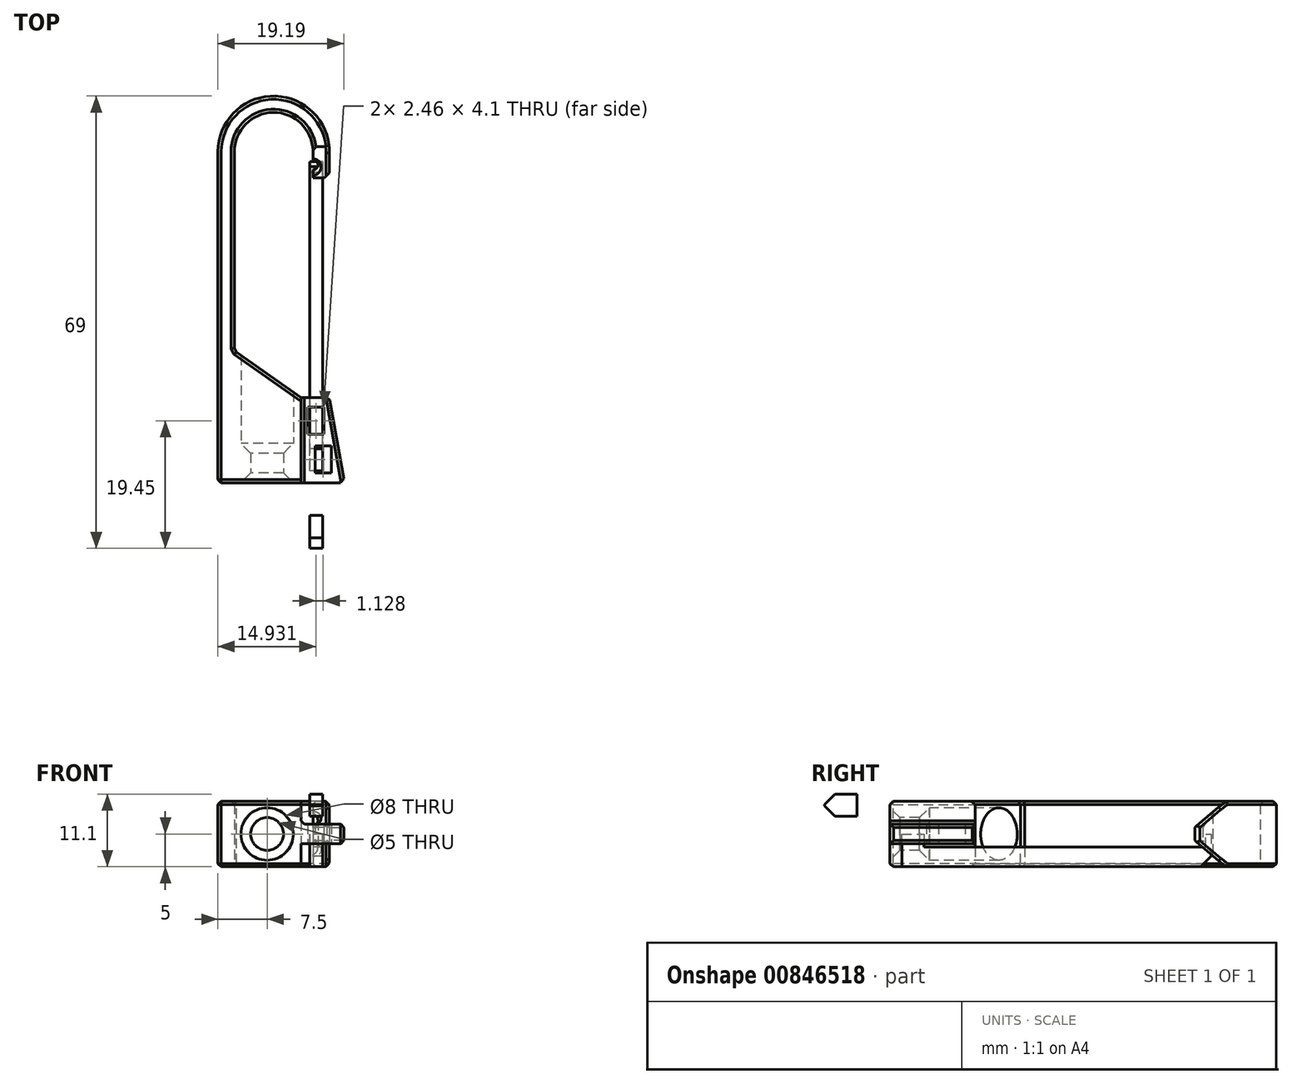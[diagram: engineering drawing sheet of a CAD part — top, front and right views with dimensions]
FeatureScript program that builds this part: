
annotation { "Feature Type Name" : "Feature", "Feature Type Description" : "" }
export const myFeature = defineFeature(function(context is Context, id is Id, definition is map)
    precondition{}
    {
        {
            var Q0;
            Q0=qCreatedBy(makeId("Top.planeOp"),FACE);
            var sketch = newSketch(context, id + "F0", { "sketchPlane" : qUnion([Q0])});
            skCircle(sketch, "E0", {"center": v(-1, -1.5) * mm, "radius": 4 * mm});
            skLineSegment(sketch, "E1.bottom", {"start": v(-8.5, 3.5) * mm, "end": v(8.5, 3.5) * mm});
            skLineSegment(sketch, "E1.top", {"start": v(-8.5, -6.5) * mm, "end": v(8.5, -6.5) * mm});
            skLineSegment(sketch, "E1.left", {"start": v(-8.5, 3.5) * mm, "end": v(-8.5, -6.5) * mm});
            skLineSegment(sketch, "E1.right", {"start": v(8.5, 3.5) * mm, "end": v(8.5, -6.5) * mm});
            skPoint(sketch, "E1.middle", {"position": v(0, -1.5) * mm});
            skCircle(sketch, "E2", {"center": v(-1, -1.5) * mm, "radius": 2.5 * mm});
            skSolve(sketch);
        }
        {
            var Q0;
            Q0=qCreatedBy(makeId("Front.planeOp"),FACE);
            cPlane(context, id + "F1", {"entities" : qUnion([Q0]), "cplaneType" : CPlaneType.OFFSET, "offset" : 3.5 * mm, "oppositeDirection" : true, "width" : 150 * mm, "height" : 150 * mm});
        }
        {
            var Q0;
            Q0=qCreatedBy(id+"F1.planeOp",FACE);
            var sketch = newSketch(context, id + "F2", { "sketchPlane" : qUnion([Q0])});
            skLineSegment(sketch, "E3", {"start": v(0, 0) * mm, "end": v(8.5, 0) * mm});
            skLineSegment(sketch, "E4.MirrorCS", {"start": v(0, 0) * mm, "end": v(-8.5, 0) * mm});
            skLineSegment(sketch, "E5", {"start": v(8.5, 0) * mm, "end": v(8.5, 13) * mm});
            skLineSegment(sketch, "E6", {"start": v(8.5, 13) * mm, "end": v(4.2, 13) * mm});
            skLineSegment(sketch, "E7", {"start": v(4.2, 13) * mm, "end": v(-6, 20.14) * mm});
            skLineSegment(sketch, "E8", {"start": v(-8.5, 0) * mm, "end": v(-8.5, 50.5) * mm});
            skLineSegment(sketch, "E9", {"start": v(-6, 20.14) * mm, "end": v(-6, 50.5) * mm});
            skLineSegment(sketch, "E10", {"start": v(-6, 50.5) * mm, "end": v(0, 50.5) * mm});
            skArc(sketch, "E11", {"start": v(8.5, 50.5) * mm, "mid": v(0, 59) * mm, "end": v(-8.5, 50.5) * mm});
            skArc(sketch, "E12", {"start": v(6, 50.5) * mm, "mid": v(0, 56.5) * mm, "end": v(-6, 50.5) * mm});
            skLineSegment(sketch, "E13", {"start": v(0, 50.5) * mm, "end": v(8.5, 50.5) * mm});
            skLineSegment(sketch, "E14", {"start": v(6, 50.5) * mm, "end": v(6, 46.5) * mm});
            skLineSegment(sketch, "E15.bottom", {"start": v(6, 46.5) * mm, "end": v(8.5, 46.5) * mm});
            skLineSegment(sketch, "E15.top", {"start": v(6, 50.5) * mm, "end": v(8.5, 50.5) * mm});
            skLineSegment(sketch, "E15.left", {"start": v(6, 46.5) * mm, "end": v(6, 50.5) * mm});
            skLineSegment(sketch, "E15.right", {"start": v(8.5, 46.5) * mm, "end": v(8.5, 50.5) * mm});
            skCircle(sketch, "E16", {"center": v(8.5, 48.5) * mm, "radius": 0.75 * mm});
            skLineSegment(sketch, "E17", {"start": v(8.5, 13) * mm, "end": v(10.8, 0) * mm});
            skLineSegment(sketch, "E18", {"start": v(10.8, 0) * mm, "end": v(8.5, 0) * mm});
            skLineSegment(sketch, "E19", {"start": v(4.2, 13) * mm, "end": v(4.2, 0) * mm});
            skLineSegment(sketch, "E20.0", {"start": v(5.2, 12) * mm, "end": v(5.2, 0) * mm});
            skLineSegment(sketch, "E20.1", {"start": v(7.66, 12) * mm, "end": v(5.2, 12) * mm});
            skLineSegment(sketch, "E20.2", {"start": v(7.66, 12) * mm, "end": v(9.6, 1) * mm});
            skLineSegment(sketch, "E20.3", {"start": v(9.6, 1) * mm, "end": v(8.5, 1) * mm});
            skLineSegment(sketch, "E21", {"start": v(8.5, 1) * mm, "end": v(5.2, 1) * mm});
            skLineSegment(sketch, "E22", {"start": v(5.2, 12) * mm, "end": v(7.14, 1) * mm});
            skCircle(sketch, "E23", {"center": v(6, 48.5) * mm, "radius": 0.75 * mm});
            skLineSegment(sketch, "E24.0", {"start": v(8.5, 11.5) * mm, "end": v(4.2, 11.5) * mm});
            skLineSegment(sketch, "E25.0", {"start": v(0, 1.5) * mm, "end": v(8.5, 1.5) * mm});
            skLineSegment(sketch, "E25.1", {"start": v(10.8, 1.5) * mm, "end": v(8.5, 1.5) * mm});
            skLineSegment(sketch, "E26", {"start": v(8.79, 5.6) * mm, "end": v(8.79, 1) * mm});
            skLineSegment(sketch, "E27", {"start": v(8.79, 5.6) * mm, "end": v(6.33, 5.6) * mm});
            skLineSegment(sketch, "E28", {"start": v(7.66, 12) * mm, "end": v(7.66, 7.4) * mm});
            skLineSegment(sketch, "E29", {"start": v(7.66, 7.4) * mm, "end": v(5.2, 7.4) * mm});
            skLineSegment(sketch, "E30", {"start": v(6.33, 5.6) * mm, "end": v(6.33, 1) * mm});
            skSolve(sketch);
        }
        {
            var Q0;
            {var subQ1=sQuery(id+"F2.wireOp",EDGE,"E6");Q0=makeQuery(id+"F2.imprint","IMPRINT",FACE,{"disambiguationData":[TD([[makeQuery(id+"F2.imprint","IMPRINT",EDGE,{"derivedFrom":subQ1}),1.0]])]});}
            var Q1;
            {var subQ0=sQuery(id+"F2.wireOp",EDGE,"E24.0");var subQ1=sQuery(id+"F2.wireOp",EDGE,"E19");var subQ2=makeQuery(id+"F2.imprint","INTERSECT",VERTEX,{"derivedFrom":[subQ1,subQ0]});Q1=makeQuery(id+"F2.imprint","IMPRINT",FACE,{"disambiguationData":[TD([[makeQuery(id+"F2.imprint","IMPRINT",EDGE,{"disambiguationData":[TD([[subQ2,-1.0]])],"derivedFrom":subQ1}),1.0]])]});}
            var Q2;
            {var subQ4=sQuery(id+"F2.wireOp",EDGE,"E3");var subQ6=sQuery(id+"F2.wireOp",EDGE,"E19");var subQ7=makeQuery(id+"F2.imprint","INTERSECT",VERTEX,{"derivedFrom":[subQ4,subQ6]});Q2=makeQuery(id+"F2.imprint","IMPRINT",FACE,{"disambiguationData":[TD([[makeQuery(id+"F2.imprint","IMPRINT",EDGE,{"disambiguationData":[TD([[subQ7,-1.0]])],"derivedFrom":subQ4}),1.0]])]});}
            var Q3;
            {var subQ0=sQuery(id+"F2.wireOp",EDGE,"E20.0");var subQ1=sQuery(id+"F2.wireOp",EDGE,"E3");var subQ2=makeQuery(id+"F2.imprint","INTERSECT",VERTEX,{"derivedFrom":[subQ1,subQ0]});Q3=makeQuery(id+"F2.imprint","IMPRINT",FACE,{"disambiguationData":[TD([[makeQuery(id+"F2.imprint","IMPRINT",EDGE,{"disambiguationData":[TD([[subQ2,1.0]])],"derivedFrom":subQ0}),1.0]])]});}
            var Q4;
            {var subQ0=sQuery(id+"F2.wireOp",EDGE,"E18");Q4=makeQuery(id+"F2.imprint","IMPRINT",FACE,{"disambiguationData":[TD([[makeQuery(id+"F2.imprint","IMPRINT",EDGE,{"derivedFrom":subQ0}),-1.0]])]});}
            var Q5;
            {var subQ2=sQuery(id+"F2.wireOp",EDGE,"E5");var subQ6=makeQuery(id+"F2.imprint","INTERSECT",VERTEX,{"derivedFrom":[subQ2,sQuery(id+"F2.wireOp",EDGE,"E24.0")]});Q5=makeQuery(id+"F2.imprint","IMPRINT",FACE,{"disambiguationData":[TD([[makeQuery(id+"F2.imprint","IMPRINT",EDGE,{"disambiguationData":[TD([[subQ6,1.0]])],"derivedFrom":subQ2}),-1.0]])]});}
            var Q6;
            {var subQ4=sQuery(id+"F2.wireOp",EDGE,"E4.MirrorCS");Q6=makeQuery(id+"F2.imprint","IMPRINT",FACE,{"disambiguationData":[TD([[makeQuery(id+"F2.imprint","IMPRINT",EDGE,{"derivedFrom":subQ4}),-1.0]])]});}
            var Q7;
            {var subQ5=sQuery(id+"F2.wireOp",EDGE,"E5");var subQ7=sQuery(id+"F2.wireOp",EDGE,"E27");var subQ13=makeQuery(id+"F2.imprint","INTERSECT",VERTEX,{"derivedFrom":[subQ5,subQ7]});Q7=makeQuery(id+"F2.imprint","IMPRINT",FACE,{"disambiguationData":[TD([[makeQuery(id+"F2.imprint","IMPRINT",EDGE,{"disambiguationData":[TD([[subQ13,-1.0]])],"derivedFrom":subQ5}),1.0]])]});}
            var Q8;
            {var subQ1=sQuery(id+"F2.wireOp",EDGE,"E20.0");var subQ7=sQuery(id+"F2.wireOp",EDGE,"E29");var subQ9=makeQuery(id+"F2.imprint","INTERSECT",VERTEX,{"derivedFrom":[subQ1,subQ7]});Q8=makeQuery(id+"F2.imprint","IMPRINT",FACE,{"disambiguationData":[TD([[makeQuery(id+"F2.imprint","IMPRINT",EDGE,{"disambiguationData":[TD([[subQ9,-1.0]])],"derivedFrom":subQ1}),1.0]])]});}
            var Q9;
            {var subQ1=sQuery(id+"F2.wireOp",EDGE,"E20.2");var subQ3=sQuery(id+"F2.wireOp",EDGE,"E24.0");var subQ4=makeQuery(id+"F2.imprint","INTERSECT",VERTEX,{"derivedFrom":[subQ1,subQ3]});Q9=makeQuery(id+"F2.imprint","IMPRINT",FACE,{"disambiguationData":[TD([[makeQuery(id+"F2.imprint","IMPRINT",EDGE,{"disambiguationData":[TD([[subQ4,-1.0]])],"derivedFrom":subQ3}),-1.0]])]});}
            var Q10;
            {var subQ0=sQuery(id+"F2.wireOp",EDGE,"E24.0");var subQ1=sQuery(id+"F2.wireOp",EDGE,"E5");var subQ2=makeQuery(id+"F2.imprint","INTERSECT",VERTEX,{"derivedFrom":[subQ1,subQ0]});Q10=makeQuery(id+"F2.imprint","IMPRINT",FACE,{"disambiguationData":[TD([[makeQuery(id+"F2.imprint","IMPRINT",EDGE,{"disambiguationData":[TD([[subQ2,1.0]])],"derivedFrom":subQ1}),1.0]])]});}
            var Q11;
            {var subQ0=sQuery(id+"F2.wireOp",EDGE,"E21");var subQ1=sQuery(id+"F2.wireOp",EDGE,"E20.0");var subQ2=makeQuery(id+"F2.imprint","INTERSECT",VERTEX,{"derivedFrom":[subQ1,subQ0]});Q11=makeQuery(id+"F2.imprint","IMPRINT",FACE,{"disambiguationData":[TD([[makeQuery(id+"F2.imprint","IMPRINT",EDGE,{"disambiguationData":[TD([[subQ2,1.0]])],"derivedFrom":subQ1}),1.0]])]});}
            var Q12;
            {var subQ4=sQuery(id+"F2.wireOp",EDGE,"E15.bottom");Q12=makeQuery(id+"F2.imprint","IMPRINT",FACE,{"disambiguationData":[TD([[makeQuery(id+"F2.imprint","IMPRINT",EDGE,{"derivedFrom":subQ4}),1.0]])]});}
            var Q13;
            {var subQ0=sQuery(id+"F2.wireOp",EDGE,"E16");var subQ1=sQuery(id+"F2.wireOp",EDGE,"E15.right");var subQ2=makeQuery(id+"F2.imprint","INTERSECT",VERTEX,{"disambiguationData":[OD(0.0)],"derivedFrom":[subQ1,subQ0]});Q13=makeQuery(id+"F2.imprint","IMPRINT",FACE,{"disambiguationData":[TD([[makeQuery(id+"F2.imprint","IMPRINT",EDGE,{"disambiguationData":[TD([[subQ2,-1.0]])],"derivedFrom":subQ1}),1.0]])]});}
            var Q14;
            {var subQ1=sQuery(id+"F2.wireOp",EDGE,"E20.2");var subQ3=sQuery(id+"F2.wireOp",EDGE,"E25.1");var subQ4=makeQuery(id+"F2.imprint","INTERSECT",VERTEX,{"derivedFrom":[subQ1,subQ3]});Q14=makeQuery(id+"F2.imprint","IMPRINT",FACE,{"disambiguationData":[TD([[makeQuery(id+"F2.imprint","IMPRINT",EDGE,{"disambiguationData":[TD([[subQ4,-1.0]])],"derivedFrom":subQ3}),-1.0]])]});}
            var Q15;
            {var subQ0=sQuery(id+"F2.wireOp",EDGE,"E20.3");var subQ1=sQuery(id+"F2.wireOp",EDGE,"E20.2");var subQ2=makeQuery(id+"F2.imprint","INTERSECT",VERTEX,{"derivedFrom":[subQ1,subQ0]});Q15=makeQuery(id+"F2.imprint","IMPRINT",FACE,{"disambiguationData":[TD([[makeQuery(id+"F2.imprint","IMPRINT",EDGE,{"disambiguationData":[TD([[subQ2,1.0]])],"derivedFrom":subQ1}),-1.0]])]});}
            var Q16;
            {var subQ0=sQuery(id+"F2.wireOp",EDGE,"E27");var subQ1=sQuery(id+"F2.wireOp",EDGE,"E5");var subQ2=makeQuery(id+"F2.imprint","INTERSECT",VERTEX,{"derivedFrom":[subQ1,subQ0]});Q16=makeQuery(id+"F2.imprint","IMPRINT",FACE,{"disambiguationData":[TD([[makeQuery(id+"F2.imprint","IMPRINT",EDGE,{"disambiguationData":[TD([[subQ2,-1.0]])],"derivedFrom":subQ1}),-1.0]])]});}
            var Q17;
            {var subQ0=sQuery(id+"F2.wireOp",EDGE,"E22");var subQ1=sQuery(id+"F2.wireOp",EDGE,"E21");var subQ2=makeQuery(id+"F2.imprint","INTERSECT",VERTEX,{"derivedFrom":[subQ1,subQ0]});Q17=makeQuery(id+"F2.imprint","IMPRINT",FACE,{"disambiguationData":[TD([[makeQuery(id+"F2.imprint","IMPRINT",EDGE,{"disambiguationData":[TD([[subQ2,-1.0]])],"derivedFrom":subQ1}),-1.0]])]});}
            var Q18;
            {var subQ0=sQuery(id+"F2.wireOp",EDGE,"E21");var subQ5=sQuery(id+"F2.wireOp",EDGE,"E22");var subQ7=makeQuery(id+"F2.imprint","INTERSECT",VERTEX,{"derivedFrom":[subQ0,subQ5]});Q18=makeQuery(id+"F2.imprint","IMPRINT",FACE,{"disambiguationData":[TD([[makeQuery(id+"F2.imprint","IMPRINT",EDGE,{"disambiguationData":[TD([[subQ7,1.0]])],"derivedFrom":subQ5}),1.0]])]});}
            var Q19;
            {var subQ0=sQuery(id+"F2.wireOp",EDGE,"E20.3");var subQ5=sQuery(id+"F2.wireOp",EDGE,"E26");var subQ6=makeQuery(id+"F2.imprint","INTERSECT",VERTEX,{"derivedFrom":[subQ0,subQ5]});Q19=makeQuery(id+"F2.imprint","IMPRINT",FACE,{"disambiguationData":[TD([[makeQuery(id+"F2.imprint","IMPRINT",EDGE,{"disambiguationData":[TD([[subQ6,1.0]])],"derivedFrom":subQ5}),-1.0]])]});}
            var Q20;
            {var subQ0=sQuery(id+"F2.wireOp",EDGE,"E20.1");Q20=makeQuery(id+"F2.imprint","IMPRINT",FACE,{"disambiguationData":[TD([[makeQuery(id+"F2.imprint","IMPRINT",EDGE,{"derivedFrom":subQ0}),1.0]])]});}
            var Q21;
            {var subQ1=sQuery(id+"F2.wireOp",EDGE,"E20.0");var subQ3=sQuery(id+"F2.wireOp",EDGE,"E24.0");var subQ4=makeQuery(id+"F2.imprint","INTERSECT",VERTEX,{"derivedFrom":[subQ1,subQ3]});Q21=makeQuery(id+"F2.imprint","IMPRINT",FACE,{"disambiguationData":[TD([[makeQuery(id+"F2.imprint","IMPRINT",EDGE,{"disambiguationData":[TD([[subQ4,1.0]])],"derivedFrom":subQ3}),-1.0]])]});}
            var Q22;
            {var subQ1=sQuery(id+"F2.wireOp",EDGE,"E20.2");var subQ3=sQuery(id+"F2.wireOp",EDGE,"E24.0");var subQ4=makeQuery(id+"F2.imprint","INTERSECT",VERTEX,{"derivedFrom":[subQ1,subQ3]});Q22=makeQuery(id+"F2.imprint","IMPRINT",FACE,{"disambiguationData":[TD([[makeQuery(id+"F2.imprint","IMPRINT",EDGE,{"disambiguationData":[TD([[subQ4,-1.0]])],"derivedFrom":subQ3}),-1.0]])]});}
            extrude(context, id + "F3", {"entities" : qUnion([Q0, Q1, Q2, Q3, Q4, Q5, Q6, Q7, Q8, Q9, Q10, Q11, Q12, Q13, Q14, Q15, Q16, Q17, Q18, Q19, Q20, Q21, Q22]), "depth" : 10 * mm, "offsetDistance" : 25 * mm});
        }
        {
            var Q0;
            Q0=makeQuery(id+"F0.imprint","IMPRINT",FACE,{"disambiguationData":[TD([[makeQuery(id+"F0.imprint","IMPRINT",EDGE,{"derivedFrom":sQuery(id+"F0.wireOp",EDGE,"E0")}),1.0]])]});
            var Q1;
            Q1=makeQuery(id+"F0.imprint","IMPRINT",FACE,{"disambiguationData":[TD([[makeQuery(id+"F0.imprint","IMPRINT",EDGE,{"derivedFrom":sQuery(id+"F0.wireOp",EDGE,"E2")}),1.0]])]});
            extrude(context, id + "F4", {"entities" : qUnion([Q0, Q1]), "operationType" : NewBodyOperationType.REMOVE, "depth" : 25 * mm, "offsetDistance" : 25 * mm});
        }
        {
            var Q0;
            Q0=makeQuery(id+"F0.imprint","IMPRINT",FACE,{"disambiguationData":[TD([[makeQuery(id+"F0.imprint","IMPRINT",EDGE,{"derivedFrom":sQuery(id+"F0.wireOp",EDGE,"E0")}),1.0]])]});
            extrude(context, id + "F5", {"entities" : qUnion([Q0]), "operationType" : NewBodyOperationType.ADD, "depth" : 6 * mm, "offsetDistance" : 25 * mm});
        }
        {
            var Q0;
            Q0=makeQuery(id+"F3.opExtrude","CAP_EDGE",EDGE,{"disambiguationData":[OSD([sQuery(id+"F2.wireOp",EDGE,"E15.bottom")])],"isStart":false});
            var Q1;
            Q1=makeQuery(id+"F3.opExtrude","CAP_EDGE",EDGE,{"disambiguationData":[OSD([sQuery(id+"F2.wireOp",EDGE,"E15.bottom")])],"isStart":true});
            chamfer(context, id + "F6", {"entities" : qUnion([Q0, Q1]), "chamferType" : ChamferType.OFFSET_ANGLE, "width" : 4 * mm, "oppositeDirection" : true, "angle" : 50 * degree, "tangentPropagation" : true});
        }
        {
            var Q0;
            Q0=makeQuery(id+"F5.opExtrude","CAP_EDGE",EDGE,{"disambiguationData":[OSD([sQuery(id+"F0.wireOp",EDGE,"E2")])],"isStart":true});
            var Q1;
            Q1=makeQuery(id+"F5.opExtrude","CAP_EDGE",EDGE,{"disambiguationData":[OSD([sQuery(id+"F0.wireOp",EDGE,"E2")])],"isStart":false});
            chamfer(context, id + "F7", {"entities" : qUnion([Q0, Q1]), "width" : 1.5 * mm, "tangentPropagation" : true});
        }
        {
            var Q0;
            Q0=makeQuery(id+"F3.opExtrude","SWEPT_EDGE",EDGE,{"disambiguationData":[OSD([sQuery(id+"F2.wireOp",EDGE,"E7"),sQuery(id+"F2.wireOp",EDGE,"E9")])]});
            var Q1;
            Q1=makeQuery(id+"F3.opExtrude","SWEPT_EDGE",EDGE,{"disambiguationData":[OSD([sQuery(id+"F2.wireOp",EDGE,"E15.bottom"),sQuery(id+"F2.wireOp",EDGE,"E15.right")])]});
            chamfer(context, id + "F8", {"entities" : qUnion([Q0, Q1]), "width" : .8 * mm, "tangentPropagation" : true});
        }
        {
            var Q0;
            Q0=qCreatedBy(id+"F1.planeOp",FACE);
            var sketch = newSketch(context, id + "F9", { "sketchPlane" : qUnion([Q0])});
            skLineSegment(sketch, "E31", {"start": v(0, 0) * mm, "end": v(4.2, 0) * mm});
            skLineSegment(sketch, "E32", {"start": v(4.2, 0) * mm, "end": v(11.2, 0) * mm});
            skLineSegment(sketch, "E33", {"start": v(4.2, 0) * mm, "end": v(4.2, 15.17) * mm});
            skLineSegment(sketch, "E34.bottom", {"start": v(4.2, 15.17) * mm, "end": v(11.2, 15.17) * mm});
            skLineSegment(sketch, "E34.left", {"start": v(4.2, 15.17) * mm, "end": v(4.2, 0) * mm});
            skLineSegment(sketch, "E34.right", {"start": v(11.2, 15.17) * mm, "end": v(11.2, 0) * mm});
            skSolve(sketch);
        }
        {
            var Q0;
            Q0=qSketchRegion(id+"F9",true);
            extrude(context, id + "F10", {"entities" : qUnion([Q0]), "operationType" : NewBodyOperationType.REMOVE, "depth" : 3.5 * mm, "offsetDistance" : 25 * mm});
        }
        {
            var Q0;
            Q0=qCreatedBy(id+"F1.planeOp",FACE);
            cPlane(context, id + "F11", {"entities" : qUnion([Q0]), "cplaneType" : CPlaneType.OFFSET, "offset" : 10 * mm, "width" : 150 * mm, "height" : 150 * mm});
        }
        {
            var Q0;
            Q0=qCreatedBy(id+"F11.planeOp",FACE);
            var sketch = newSketch(context, id + "F12", { "sketchPlane" : qUnion([Q0])});
            skLineSegment(sketch, "E35", {"start": v(0, 0) * mm, "end": v(4.2, 0) * mm});
            skLineSegment(sketch, "E36", {"start": v(4.2, 0) * mm, "end": v(11.2, 0) * mm});
            skLineSegment(sketch, "E37", {"start": v(11.2, 0) * mm, "end": v(11.2, 14.54) * mm});
            skLineSegment(sketch, "E38.bottom", {"start": v(11.2, 14.54) * mm, "end": v(4.2, 14.54) * mm});
            skLineSegment(sketch, "E38.top", {"start": v(11.2, 0) * mm, "end": v(4.2, 0) * mm});
            skLineSegment(sketch, "E38.left", {"start": v(11.2, 14.54) * mm, "end": v(11.2, 0) * mm});
            skLineSegment(sketch, "E38.right", {"start": v(4.2, 14.54) * mm, "end": v(4.2, 0) * mm});
            skSolve(sketch);
        }
        {
            var Q0;
            Q0=qSketchRegion(id+"F12",true);
            extrude(context, id + "F13", {"entities" : qUnion([Q0]), "operationType" : NewBodyOperationType.REMOVE, "oppositeDirection" : true, "depth" : 3.5 * mm, "offsetDistance" : 25 * mm});
        }
        {
            var Q0;
            Q0=makeQuery(id+"F13.boolean.opBoolean","INTERSECT",EDGE,{"derivedFrom":[makeQuery(id+"F3.opExtrude","SWEPT_FACE",FACE,{"disambiguationData":[OSD([sQuery(id+"F2.wireOp",EDGE,"E17")])]}),makeQuery(id+"F13.opExtrude","CAP_FACE",FACE,{"disambiguationData":[OSD([sQuery(id+"F12.wireOp",EDGE,"E38.bottom"),sQuery(id+"F12.wireOp",EDGE,"E38.top"),sQuery(id+"F12.wireOp",EDGE,"E38.left"),sQuery(id+"F12.wireOp",EDGE,"E38.right")])],"isStart":false})]});
            var Q1;
            Q1=makeQuery(id+"F10.boolean.opBoolean","INTERSECT",EDGE,{"derivedFrom":[makeQuery(id+"F3.opExtrude","SWEPT_FACE",FACE,{"disambiguationData":[OSD([sQuery(id+"F2.wireOp",EDGE,"E17")])]}),makeQuery(id+"F10.opExtrude","CAP_FACE",FACE,{"disambiguationData":[OSD([sQuery(id+"F9.wireOp",EDGE,"E34.bottom"),sQuery(id+"F9.wireOp",EDGE,"E32"),sQuery(id+"F9.wireOp",EDGE,"E34.left"),sQuery(id+"F9.wireOp",EDGE,"E34.right")])],"isStart":false})]});
            var Q2;
            Q2=makeQuery(id+"F3.opExtrude","CAP_EDGE",EDGE,{"disambiguationData":[OSD([sQuery(id+"F2.wireOp",EDGE,"E8")])],"isStart":false});
            var Q3;
            Q3=makeQuery(id+"F3.opExtrude","CAP_EDGE",EDGE,{"disambiguationData":[OSD([sQuery(id+"F2.wireOp",EDGE,"E8")])],"isStart":true});
            var Q4;
            Q4=makeQuery(id+"F3.opExtrude","CAP_EDGE",EDGE,{"disambiguationData":[OSD([sQuery(id+"F2.wireOp",EDGE,"E9")])],"isStart":true});
            var Q5;
            Q5=makeQuery(id+"F3.opExtrude","CAP_EDGE",EDGE,{"disambiguationData":[OSD([sQuery(id+"F2.wireOp",EDGE,"E9")])],"isStart":false});
            var Q6;
            Q6=makeQuery(id+"F3.opExtrude","CAP_EDGE",EDGE,{"disambiguationData":[OSD([sQuery(id+"F2.wireOp",EDGE,"E7")])],"isStart":false});
            var Q7;
            Q7=makeQuery(id+"F3.opExtrude","CAP_EDGE",EDGE,{"disambiguationData":[OSD([sQuery(id+"F2.wireOp",EDGE,"E7")])],"isStart":true});
            var Q8;
            {var subQ0=sQuery(id+"F2.wireOp",EDGE,"E9");var subQ1=sQuery(id+"F2.wireOp",EDGE,"E7");Q8=makeQuery(id+"F8.opChamfer","BLEND_EDGE",EDGE,{"blendedFrom":[makeQuery(id+"F3.opExtrude","SWEPT_EDGE",EDGE,{"disambiguationData":[OSD([subQ1,subQ0])]}),makeQuery(id+"F3.opExtrude","CAP_FACE",FACE,{"disambiguationData":[OSD([sQuery(id+"F2.wireOp",EDGE,"E3"),sQuery(id+"F2.wireOp",EDGE,"E4.MirrorCS"),sQuery(id+"F2.wireOp",EDGE,"E6"),subQ1,sQuery(id+"F2.wireOp",EDGE,"E8"),subQ0,sQuery(id+"F2.wireOp",EDGE,"E11"),sQuery(id+"F2.wireOp",EDGE,"E12"),sQuery(id+"F2.wireOp",EDGE,"E15.bottom"),sQuery(id+"F2.wireOp",EDGE,"E15.left"),sQuery(id+"F2.wireOp",EDGE,"E15.right"),sQuery(id+"F2.wireOp",EDGE,"E16"),sQuery(id+"F2.wireOp",EDGE,"E17"),sQuery(id+"F2.wireOp",EDGE,"E18")])],"isStart":true})],"blendedInto":[makeQuery(id+"F3.opExtrude","CAP_FACE",FACE,{"disambiguationData":[OSD([sQuery(id+"F2.wireOp",EDGE,"E3"),sQuery(id+"F2.wireOp",EDGE,"E4.MirrorCS"),sQuery(id+"F2.wireOp",EDGE,"E6"),subQ1,sQuery(id+"F2.wireOp",EDGE,"E8"),subQ0,sQuery(id+"F2.wireOp",EDGE,"E11"),sQuery(id+"F2.wireOp",EDGE,"E12"),sQuery(id+"F2.wireOp",EDGE,"E15.bottom"),sQuery(id+"F2.wireOp",EDGE,"E15.left"),sQuery(id+"F2.wireOp",EDGE,"E15.right"),sQuery(id+"F2.wireOp",EDGE,"E16"),sQuery(id+"F2.wireOp",EDGE,"E17"),sQuery(id+"F2.wireOp",EDGE,"E18")])],"isStart":true})]});}
            var Q9;
            {var subQ0=sQuery(id+"F2.wireOp",EDGE,"E9");var subQ1=sQuery(id+"F2.wireOp",EDGE,"E7");Q9=makeQuery(id+"F8.opChamfer","BLEND_EDGE",EDGE,{"blendedFrom":[makeQuery(id+"F3.opExtrude","SWEPT_EDGE",EDGE,{"disambiguationData":[OSD([subQ1,subQ0])]}),makeQuery(id+"F3.opExtrude","CAP_FACE",FACE,{"disambiguationData":[OSD([sQuery(id+"F2.wireOp",EDGE,"E3"),sQuery(id+"F2.wireOp",EDGE,"E4.MirrorCS"),sQuery(id+"F2.wireOp",EDGE,"E6"),subQ1,sQuery(id+"F2.wireOp",EDGE,"E8"),subQ0,sQuery(id+"F2.wireOp",EDGE,"E11"),sQuery(id+"F2.wireOp",EDGE,"E12"),sQuery(id+"F2.wireOp",EDGE,"E15.bottom"),sQuery(id+"F2.wireOp",EDGE,"E15.left"),sQuery(id+"F2.wireOp",EDGE,"E15.right"),sQuery(id+"F2.wireOp",EDGE,"E16"),sQuery(id+"F2.wireOp",EDGE,"E17"),sQuery(id+"F2.wireOp",EDGE,"E18")])],"isStart":false})],"blendedInto":[makeQuery(id+"F3.opExtrude","CAP_FACE",FACE,{"disambiguationData":[OSD([sQuery(id+"F2.wireOp",EDGE,"E3"),sQuery(id+"F2.wireOp",EDGE,"E4.MirrorCS"),sQuery(id+"F2.wireOp",EDGE,"E6"),subQ1,sQuery(id+"F2.wireOp",EDGE,"E8"),subQ0,sQuery(id+"F2.wireOp",EDGE,"E11"),sQuery(id+"F2.wireOp",EDGE,"E12"),sQuery(id+"F2.wireOp",EDGE,"E15.bottom"),sQuery(id+"F2.wireOp",EDGE,"E15.left"),sQuery(id+"F2.wireOp",EDGE,"E15.right"),sQuery(id+"F2.wireOp",EDGE,"E16"),sQuery(id+"F2.wireOp",EDGE,"E17"),sQuery(id+"F2.wireOp",EDGE,"E18")])],"isStart":false})]});}
            var Q10;
            Q10=makeQuery(id+"F6.opChamfer","BLEND_EDGE",EDGE,{"blendedFrom":[makeQuery(id+"F3.opExtrude","CAP_EDGE",EDGE,{"disambiguationData":[OSD([sQuery(id+"F2.wireOp",EDGE,"E15.bottom")])],"isStart":false}),makeQuery(id+"F3.opExtrude","SWEPT_FACE",FACE,{"disambiguationData":[OSD([sQuery(id+"F2.wireOp",EDGE,"E15.left")])]})],"blendedInto":[makeQuery(id+"F3.opExtrude","SWEPT_FACE",FACE,{"disambiguationData":[OSD([sQuery(id+"F2.wireOp",EDGE,"E15.left")])]})]});
            var Q11;
            Q11=makeQuery(id+"F6.opChamfer","BLEND_EDGE",EDGE,{"blendedFrom":[makeQuery(id+"F3.opExtrude","CAP_EDGE",EDGE,{"disambiguationData":[OSD([sQuery(id+"F2.wireOp",EDGE,"E15.bottom")])],"isStart":true}),makeQuery(id+"F3.opExtrude","SWEPT_FACE",FACE,{"disambiguationData":[OSD([sQuery(id+"F2.wireOp",EDGE,"E15.left")])]})],"blendedInto":[makeQuery(id+"F3.opExtrude","SWEPT_FACE",FACE,{"disambiguationData":[OSD([sQuery(id+"F2.wireOp",EDGE,"E15.left")])]})]});
            var Q12;
            {var subQ0=sQuery(id+"F2.wireOp",EDGE,"E15.right");Q12=makeQuery(id+"F6.opChamfer","BLEND_EDGE",EDGE,{"blendedFrom":[makeQuery(id+"F3.opExtrude","CAP_EDGE",EDGE,{"disambiguationData":[OSD([sQuery(id+"F2.wireOp",EDGE,"E15.bottom")])],"isStart":false}),makeQuery(id+"F3.opExtrude","SWEPT_FACE",FACE,{"disambiguationData":[OSD([subQ0]),TDD([makeQuery(id+"F2.imprint","IMPRINT",EDGE,{"disambiguationData":[TD([[makeQuery(id+"F2.imprint","INTERSECT",VERTEX,{"disambiguationData":[OD(1.0)],"derivedFrom":[subQ0,sQuery(id+"F2.wireOp",EDGE,"E16")]}),-1.0]])],"derivedFrom":subQ0})])]})],"blendedInto":[makeQuery(id+"F3.opExtrude","SWEPT_FACE",FACE,{"disambiguationData":[OSD([subQ0]),TDD([makeQuery(id+"F2.imprint","IMPRINT",EDGE,{"disambiguationData":[TD([[makeQuery(id+"F2.imprint","INTERSECT",VERTEX,{"disambiguationData":[OD(1.0)],"derivedFrom":[subQ0,sQuery(id+"F2.wireOp",EDGE,"E16")]}),-1.0]])],"derivedFrom":subQ0})])]})]});}
            var Q13;
            Q13=makeQuery(id+"F6.opChamfer","BLEND_EDGE",EDGE,{"blendedFrom":[makeQuery(id+"F3.opExtrude","CAP_EDGE",EDGE,{"disambiguationData":[OSD([sQuery(id+"F2.wireOp",EDGE,"E15.bottom")])],"isStart":false}),makeQuery(id+"F3.opExtrude","SWEPT_FACE",FACE,{"disambiguationData":[OSD([sQuery(id+"F2.wireOp",EDGE,"E16")])]})],"blendedInto":[makeQuery(id+"F3.opExtrude","SWEPT_FACE",FACE,{"disambiguationData":[OSD([sQuery(id+"F2.wireOp",EDGE,"E16")])]})]});
            var Q14;
            {var subQ0=sQuery(id+"F2.wireOp",EDGE,"E15.right");var subQ1=sQuery(id+"F2.wireOp",EDGE,"E15.bottom");Q14=makeQuery(id+"F6.opChamfer","BLEND_EDGE",EDGE,{"blendedFrom":[makeQuery(id+"F3.opExtrude","CAP_EDGE",EDGE,{"disambiguationData":[OSD([subQ1])],"isStart":false}),makeQuery(id+"F3.opExtrude","SWEPT_FACE",FACE,{"disambiguationData":[OSD([subQ0]),TDD([makeQuery(id+"F2.imprint","IMPRINT",EDGE,{"disambiguationData":[TD([[makeQuery(id+"F2.imprint","INTERSECT",VERTEX,{"derivedFrom":[subQ1,subQ0]}),-1.0]])],"derivedFrom":subQ0})])]})],"blendedInto":[makeQuery(id+"F3.opExtrude","SWEPT_FACE",FACE,{"disambiguationData":[OSD([subQ0]),TDD([makeQuery(id+"F2.imprint","IMPRINT",EDGE,{"disambiguationData":[TD([[makeQuery(id+"F2.imprint","INTERSECT",VERTEX,{"derivedFrom":[subQ1,subQ0]}),-1.0]])],"derivedFrom":subQ0})])]})]});}
            var Q15;
            {var subQ0=sQuery(id+"F2.wireOp",EDGE,"E15.right");Q15=makeQuery(id+"F6.opChamfer","BLEND_EDGE",EDGE,{"blendedFrom":[makeQuery(id+"F3.opExtrude","CAP_EDGE",EDGE,{"disambiguationData":[OSD([sQuery(id+"F2.wireOp",EDGE,"E15.bottom")])],"isStart":true}),makeQuery(id+"F3.opExtrude","SWEPT_FACE",FACE,{"disambiguationData":[OSD([subQ0]),TDD([makeQuery(id+"F2.imprint","IMPRINT",EDGE,{"disambiguationData":[TD([[makeQuery(id+"F2.imprint","INTERSECT",VERTEX,{"disambiguationData":[OD(1.0)],"derivedFrom":[subQ0,sQuery(id+"F2.wireOp",EDGE,"E16")]}),-1.0]])],"derivedFrom":subQ0})])]})],"blendedInto":[makeQuery(id+"F3.opExtrude","SWEPT_FACE",FACE,{"disambiguationData":[OSD([subQ0]),TDD([makeQuery(id+"F2.imprint","IMPRINT",EDGE,{"disambiguationData":[TD([[makeQuery(id+"F2.imprint","INTERSECT",VERTEX,{"disambiguationData":[OD(1.0)],"derivedFrom":[subQ0,sQuery(id+"F2.wireOp",EDGE,"E16")]}),-1.0]])],"derivedFrom":subQ0})])]})]});}
            var Q16;
            Q16=makeQuery(id+"F6.opChamfer","BLEND_EDGE",EDGE,{"blendedFrom":[makeQuery(id+"F3.opExtrude","CAP_EDGE",EDGE,{"disambiguationData":[OSD([sQuery(id+"F2.wireOp",EDGE,"E15.bottom")])],"isStart":true}),makeQuery(id+"F3.opExtrude","SWEPT_FACE",FACE,{"disambiguationData":[OSD([sQuery(id+"F2.wireOp",EDGE,"E16")])]})],"blendedInto":[makeQuery(id+"F3.opExtrude","SWEPT_FACE",FACE,{"disambiguationData":[OSD([sQuery(id+"F2.wireOp",EDGE,"E16")])]})]});
            var Q17;
            {var subQ0=sQuery(id+"F2.wireOp",EDGE,"E15.right");var subQ1=sQuery(id+"F2.wireOp",EDGE,"E15.bottom");Q17=makeQuery(id+"F6.opChamfer","BLEND_EDGE",EDGE,{"blendedFrom":[makeQuery(id+"F3.opExtrude","CAP_EDGE",EDGE,{"disambiguationData":[OSD([subQ1])],"isStart":true}),makeQuery(id+"F3.opExtrude","SWEPT_FACE",FACE,{"disambiguationData":[OSD([subQ0]),TDD([makeQuery(id+"F2.imprint","IMPRINT",EDGE,{"disambiguationData":[TD([[makeQuery(id+"F2.imprint","INTERSECT",VERTEX,{"derivedFrom":[subQ1,subQ0]}),-1.0]])],"derivedFrom":subQ0})])]})],"blendedInto":[makeQuery(id+"F3.opExtrude","SWEPT_FACE",FACE,{"disambiguationData":[OSD([subQ0]),TDD([makeQuery(id+"F2.imprint","IMPRINT",EDGE,{"disambiguationData":[TD([[makeQuery(id+"F2.imprint","INTERSECT",VERTEX,{"derivedFrom":[subQ1,subQ0]}),-1.0]])],"derivedFrom":subQ0})])]})]});}
            var Q18;
            Q18=makeQuery(id+"F10.boolean.opBoolean","COPY",EDGE,{"derivedFrom":makeQuery(id+"F10.opExtrude","CAP_EDGE",EDGE,{"disambiguationData":[OSD([sQuery(id+"F9.wireOp",EDGE,"E34.left")])],"isStart":true})});
            var Q19;
            Q19=makeQuery(id+"F13.boolean.opBoolean","COPY",EDGE,{"derivedFrom":makeQuery(id+"F13.opExtrude","CAP_EDGE",EDGE,{"disambiguationData":[OSD([sQuery(id+"F12.wireOp",EDGE,"E38.right")])],"isStart":true})});
            var Q20;
            Q20=makeQuery(id+"F13.boolean.opBoolean","COPY",EDGE,{"derivedFrom":makeQuery(id+"F13.opExtrude","CAP_EDGE",EDGE,{"disambiguationData":[OSD([sQuery(id+"F12.wireOp",EDGE,"E38.right")])],"isStart":false})});
            var Q21;
            Q21=makeQuery(id+"F10.boolean.opBoolean","COPY",EDGE,{"derivedFrom":makeQuery(id+"F10.opExtrude","CAP_EDGE",EDGE,{"disambiguationData":[OSD([sQuery(id+"F9.wireOp",EDGE,"E34.left")])],"isStart":false})});
            var Q22;
            Q22=makeQuery(id+"F3.opExtrude","SWEPT_EDGE",EDGE,{"disambiguationData":[OSD([sQuery(id+"F2.wireOp",EDGE,"E5"),sQuery(id+"F2.wireOp",EDGE,"E6"),sQuery(id+"F2.wireOp",EDGE,"E17")])]});
            var Q23;
            Q23=makeQuery(id+"F3.opExtrude","CAP_EDGE",EDGE,{"disambiguationData":[OSD([sQuery(id+"F2.wireOp",EDGE,"E3"),sQuery(id+"F2.wireOp",EDGE,"E4.MirrorCS"),sQuery(id+"F2.wireOp",EDGE,"E18")])],"isStart":false});
            var Q24;
            Q24=makeQuery(id+"F3.opExtrude","CAP_EDGE",EDGE,{"disambiguationData":[OSD([sQuery(id+"F2.wireOp",EDGE,"E3"),sQuery(id+"F2.wireOp",EDGE,"E4.MirrorCS"),sQuery(id+"F2.wireOp",EDGE,"E18")])],"isStart":true});
            var Q25;
            Q25=makeQuery(id+"F3.opExtrude","SWEPT_EDGE",EDGE,{"disambiguationData":[OSD([sQuery(id+"F2.wireOp",EDGE,"E4.MirrorCS"),sQuery(id+"F2.wireOp",EDGE,"E8")])]});
            var Q26;
            Q26=makeQuery(id+"F3.opExtrude","SWEPT_EDGE",EDGE,{"disambiguationData":[OSD([sQuery(id+"F2.wireOp",EDGE,"E17"),sQuery(id+"F2.wireOp",EDGE,"E18")])]});
            var Q27;
            Q27=makeQuery(id+"F6.opChamfer","BLEND_EDGE",EDGE,{"blendedFrom":[makeQuery(id+"F3.opExtrude","CAP_EDGE",EDGE,{"disambiguationData":[OSD([sQuery(id+"F2.wireOp",EDGE,"E15.bottom")])],"isStart":false}),makeQuery(id+"F3.opExtrude","SWEPT_FACE",FACE,{"disambiguationData":[OSD([sQuery(id+"F2.wireOp",EDGE,"E23")])]})],"blendedInto":[makeQuery(id+"F3.opExtrude","SWEPT_FACE",FACE,{"disambiguationData":[OSD([sQuery(id+"F2.wireOp",EDGE,"E23")])]})]});
            var Q28;
            Q28=makeQuery(id+"F6.opChamfer","BLEND_EDGE",EDGE,{"blendedFrom":[makeQuery(id+"F3.opExtrude","CAP_EDGE",EDGE,{"disambiguationData":[OSD([sQuery(id+"F2.wireOp",EDGE,"E15.bottom")])],"isStart":true}),makeQuery(id+"F3.opExtrude","SWEPT_FACE",FACE,{"disambiguationData":[OSD([sQuery(id+"F2.wireOp",EDGE,"E23")])]})],"blendedInto":[makeQuery(id+"F3.opExtrude","SWEPT_FACE",FACE,{"disambiguationData":[OSD([sQuery(id+"F2.wireOp",EDGE,"E23")])]})]});
            chamfer(context, id + "F14", {"entities" : qUnion([Q0, Q1, Q2, Q3, Q4, Q5, Q6, Q7, Q8, Q9, Q10, Q11, Q12, Q13, Q14, Q15, Q16, Q17, Q18, Q19, Q20, Q21, Q22, Q23, Q24, Q25, Q26, Q27, Q28]), "width" : .5 * mm, "tangentPropagation" : true});
        }
        {
            var Q0;
            Q0=qCreatedBy(makeId("Right.planeOp"),FACE);
            cPlane(context, id + "F15", {"entities" : qUnion([Q0]), "cplaneType" : CPlaneType.OFFSET, "offset" : 5.5 * mm, "width" : 150 * mm, "height" : 150 * mm});
        }
        {
            var Q0;
            Q0=qCreatedBy(id+"F15.planeOp",FACE);
            var sketch = newSketch(context, id + "F16", { "sketchPlane" : qUnion([Q0])});
            skLineSegment(sketch, "E39", {"start": v(0, 0) * mm, "end": v(-1.5, 0) * mm});
            skLineSegment(sketch, "E40", {"start": v(-1.5, 0) * mm, "end": v(-1.5, 49) * mm});
            skLineSegment(sketch, "E41", {"start": v(-1.5, 49) * mm, "end": v(3.5, 49) * mm});
            skLineSegment(sketch, "E42", {"start": v(3.5, 49) * mm, "end": v(3.5, 0) * mm});
            skLineSegment(sketch, "E43", {"start": v(3.5, 0) * mm, "end": v(-1.5, 0) * mm});
            skLineSegment(sketch, "E44", {"start": v(-1.5, 0) * mm, "end": v(-1.5, 5.2) * mm});
            skLineSegment(sketch, "E45", {"start": v(-1.5, 5.2) * mm, "end": v(0.5, 5.2) * mm});
            skLineSegment(sketch, "E46", {"start": v(0.5, 5.2) * mm, "end": v(0.5, 48.2) * mm});
            skLineSegment(sketch, "E47", {"start": v(0.5, 48.2) * mm, "end": v(-1.5, 48.2) * mm});
            skLineSegment(sketch, "E48.MirrorCS", {"start": v(-3.5, 48.2) * mm, "end": v(-1.5, 48.2) * mm});
            skLineSegment(sketch, "E49.MirrorCS", {"start": v(-1.5, 49) * mm, "end": v(-6.5, 49) * mm});
            skLineSegment(sketch, "E50.MirrorCS", {"start": v(-6.5, 49) * mm, "end": v(-6.5, 0) * mm});
            skLineSegment(sketch, "E51", {"start": v(-6.5, 0) * mm, "end": v(-6.5, 11.1) * mm});
            skLineSegment(sketch, "E52", {"start": v(-6.5, 11.1) * mm, "end": v(-1.5, 11.1) * mm});
            skLineSegment(sketch, "E53", {"start": v(-1.5, 11.1) * mm, "end": v(-1.5, 7.7) * mm});
            skLineSegment(sketch, "E54", {"start": v(-1.5, 7.7) * mm, "end": v(-6.5, 7.7) * mm});
            skLineSegment(sketch, "E55", {"start": v(-3.5, 48.2) * mm, "end": v(-3.5, 11.1) * mm});
            skPoint(sketch, "E55.endSnap0", {"position": v(-4, 11.1) * mm});
            skLineSegment(sketch, "E56", {"start": v(3.5, 0) * mm, "end": v(3.5, 1.8) * mm});
            skLineSegment(sketch, "E57", {"start": v(3.5, 1.8) * mm, "end": v(-1.5, 1.8) * mm});
            skLineSegment(sketch, "E58", {"start": v(-1.5, 5.2) * mm, "end": v(-2.5, 5.2) * mm});
            skLineSegment(sketch, "E59.bottom", {"start": v(-2.5, 5.2) * mm, "end": v(-1.5, 5.2) * mm});
            skLineSegment(sketch, "E59.top", {"start": v(-2.5, 1.8) * mm, "end": v(-1.5, 1.8) * mm});
            skLineSegment(sketch, "E59.left", {"start": v(-2.5, 5.2) * mm, "end": v(-2.5, 1.8) * mm});
            skLineSegment(sketch, "E59.right", {"start": v(-1.5, 5.2) * mm, "end": v(-1.5, 1.8) * mm});
            skLineSegment(sketch, "E60", {"start": v(-1.5, 7.7) * mm, "end": v(-0.5, 7.7) * mm});
            skLineSegment(sketch, "E61.bottom", {"start": v(-0.5, 7.7) * mm, "end": v(-1.5, 7.7) * mm});
            skLineSegment(sketch, "E61.top", {"start": v(-0.5, 11.1) * mm, "end": v(-1.5, 11.1) * mm});
            skLineSegment(sketch, "E61.left", {"start": v(-0.5, 7.7) * mm, "end": v(-0.5, 11.1) * mm});
            skLineSegment(sketch, "E61.right", {"start": v(-1.5, 7.7) * mm, "end": v(-1.5, 11.1) * mm});
            skSolve(sketch);
        }
        {
            var Q0;
            {var subQ0=sQuery(id+"F16.wireOp",EDGE,"E50.MirrorCS");Q0=makeQuery(id+"F16.imprint","IMPRINT",FACE,{"disambiguationData":[TD([[makeQuery(id+"F16.imprint","IMPRINT",EDGE,{"derivedFrom":subQ0}),1.0]])]});}
            var Q1;
            {var subQ0=sQuery(id+"F16.wireOp",EDGE,"E53");Q1=makeQuery(id+"F16.imprint","IMPRINT",FACE,{"disambiguationData":[TD([[makeQuery(id+"F16.imprint","IMPRINT",EDGE,{"derivedFrom":subQ0}),-1.0]])]});}
            var Q2;
            Q2=makeQuery(id+"F16.imprint","IMPRINT",FACE,{"disambiguationData":[TD([[makeQuery(id+"F16.imprint","IMPRINT",EDGE,{"derivedFrom":sQuery(id+"F16.wireOp",EDGE,"E41")}),-1.0]])]});
            var Q3;
            {var subQ0=sQuery(id+"F16.wireOp",EDGE,"E54");Q3=makeQuery(id+"F16.imprint","IMPRINT",FACE,{"disambiguationData":[TD([[makeQuery(id+"F16.imprint","IMPRINT",EDGE,{"derivedFrom":subQ0}),-1.0]])]});}
            var Q4;
            Q4=makeQuery(id+"F16.imprint","IMPRINT",FACE,{"disambiguationData":[TD([[makeQuery(id+"F16.imprint","IMPRINT",EDGE,{"derivedFrom":sQuery(id+"F16.wireOp",EDGE,"E59.bottom")}),-1.0]])]});
            var Q5;
            Q5=makeQuery(id+"F16.imprint","IMPRINT",FACE,{"disambiguationData":[TD([[makeQuery(id+"F16.imprint","IMPRINT",EDGE,{"derivedFrom":sQuery(id+"F16.wireOp",EDGE,"E61.bottom")}),-1.0]])]});
            extrude(context, id + "F17", {"entities" : qUnion([Q0, Q1, Q2, Q3, Q4, Q5]), "depth" : 2 * mm, "offsetDistance" : 25 * mm});
        }
        {
            var Q0;
            Q0=makeQuery(id+"F3.opExtrude","SWEPT_BODY",BODY,{"disambiguationData":[OSD([sQuery(id+"F2.wireOp",EDGE,"E3"),sQuery(id+"F2.wireOp",EDGE,"E4.MirrorCS"),sQuery(id+"F2.wireOp",EDGE,"E5"),sQuery(id+"F2.wireOp",EDGE,"E6"),sQuery(id+"F2.wireOp",EDGE,"E7"),sQuery(id+"F2.wireOp",EDGE,"E8"),sQuery(id+"F2.wireOp",EDGE,"E9"),sQuery(id+"F2.wireOp",EDGE,"E11"),sQuery(id+"F2.wireOp",EDGE,"E12"),sQuery(id+"F2.wireOp",EDGE,"0akQF3o6-GRSy-sqst-GOAi-R7572j4TWCA9"),sQuery(id+"F2.wireOp",EDGE,"Rr7SK3JZ-Egbp-8AZP-2McZ-Qu5wQ8jnj7ba"),sQuery(id+"F2.wireOp",EDGE,"E15.bottom"),sQuery(id+"F2.wireOp",EDGE,"E15.left"),sQuery(id+"F2.wireOp",EDGE,"E15.right"),sQuery(id+"F2.wireOp",EDGE,"E16")])]});
            var Q1;
            Q1=makeQuery(id+"F17.opExtrude","SWEPT_BODY",BODY,{"disambiguationData":[OSD([sQuery(id+"F16.wireOp",EDGE,"E41"),sQuery(id+"F16.wireOp",EDGE,"E42"),sQuery(id+"F16.wireOp",EDGE,"E44"),sQuery(id+"F16.wireOp",EDGE,"E45"),sQuery(id+"F16.wireOp",EDGE,"E46"),sQuery(id+"F16.wireOp",EDGE,"E47"),sQuery(id+"F16.wireOp",EDGE,"E48.MirrorCS"),sQuery(id+"F16.wireOp",EDGE,"E49.MirrorCS"),sQuery(id+"F16.wireOp",EDGE,"E50.MirrorCS"),sQuery(id+"F16.wireOp",EDGE,"E51"),sQuery(id+"F16.wireOp",EDGE,"E52"),sQuery(id+"F16.wireOp",EDGE,"E53"),sQuery(id+"F16.wireOp",EDGE,"E54"),sQuery(id+"F16.wireOp",EDGE,"E55"),sQuery(id+"F16.wireOp",EDGE,"E57")])]});
            var Q2;
            Q2=sQuery(id+"F0.wireOp",EDGE,"E1.bottom");
            transform(context, id + "F18", {"entities" : qUnion([Q0, Q1]), "transformType" : TransformType.ROTATION, "transformAxis" : qUnion([Q2]), "angle" : 90 * degree, "oppositeDirection" : true, "makeCopy" : false});
        }
        {
            var Q0;
            Q0=makeQuery(id+"F17.opExtrude","SWEPT_EDGE",EDGE,{"disambiguationData":[OSD([sQuery(id+"F16.wireOp",EDGE,"E49.MirrorCS"),sQuery(id+"F16.wireOp",EDGE,"E50.MirrorCS")])]});
            var Q1;
            Q1=makeQuery(id+"F17.opExtrude","SWEPT_EDGE",EDGE,{"disambiguationData":[OSD([sQuery(id+"F16.wireOp",EDGE,"E41"),sQuery(id+"F16.wireOp",EDGE,"E42")])]});
            chamfer(context, id + "F19", {"entities" : qUnion([Q0, Q1]), "width" : 1.6 * mm, "tangentPropagation" : true});
        }
    });
